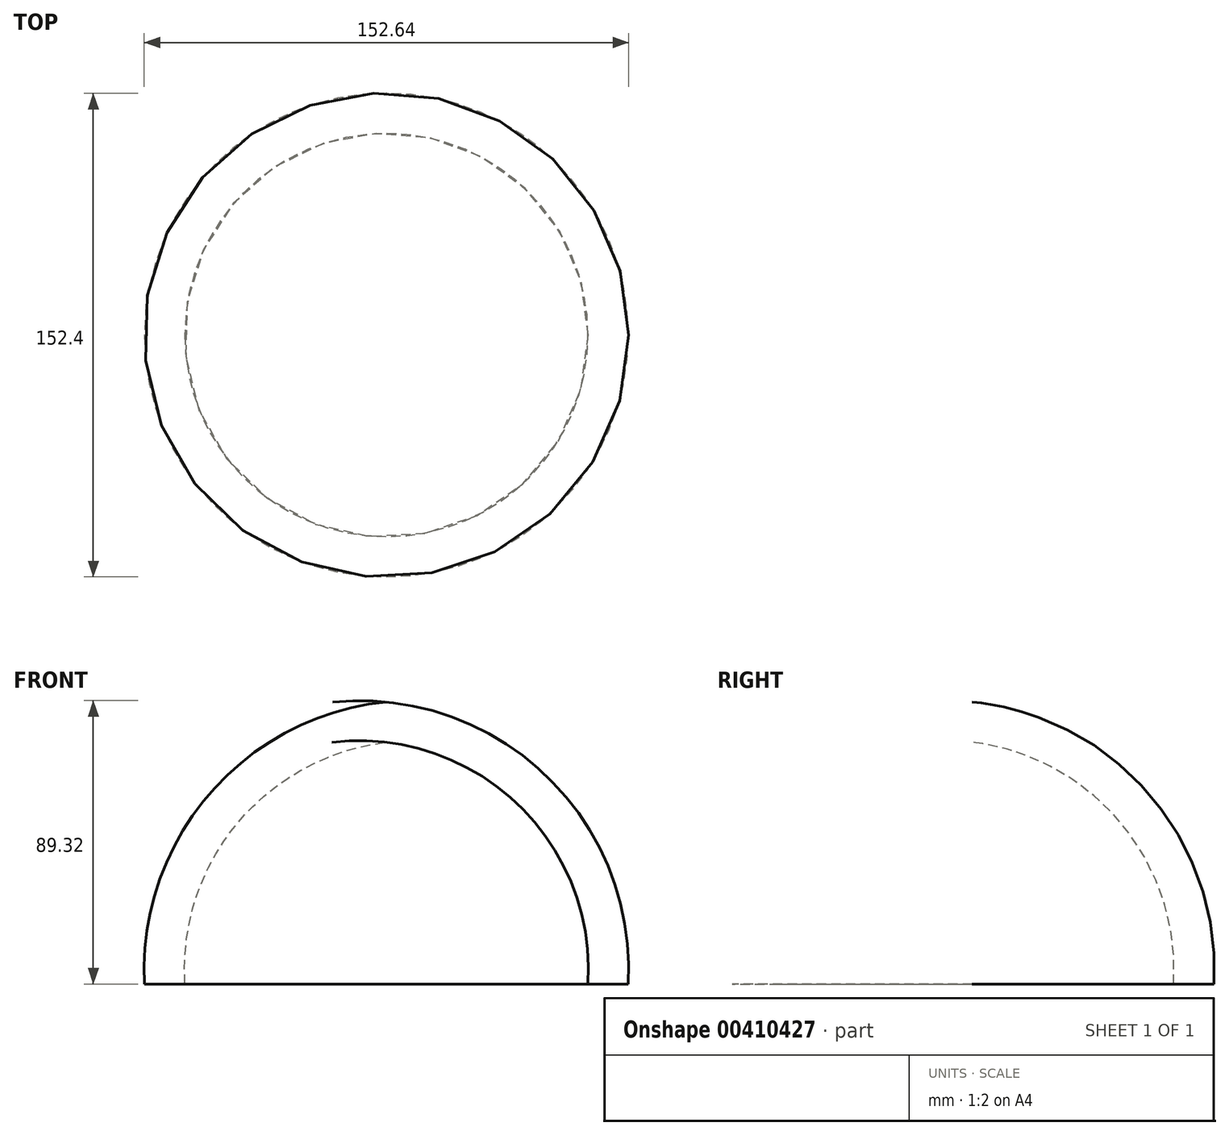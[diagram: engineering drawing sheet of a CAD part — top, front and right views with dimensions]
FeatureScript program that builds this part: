
annotation { "Feature Type Name" : "Feature", "Feature Type Description" : "" }
export const myFeature = defineFeature(function(context is Context, id is Id, definition is map)
    precondition{}
    {
        {
            var Q0;
            Q0=qCreatedBy(makeId("Front.planeOp"),FACE);
            var sketch = newSketch(context, id + "F0", { "sketchPlane" : qUnion([Q0])});
            skLineSegment(sketch, "E0", {"start": v(0, 76.2) * mm, "end": v(0, 88.9) * mm});
            skLineSegment(sketch, "E1", {"start": v(63.5, 0) * mm, "end": v(76.2, 0) * mm});
            skArc(sketch, "E2", {"start": v(76.2, 0) * mm, "mid": v(55.92, 59.72) * mm, "end": v(0, 88.9) * mm});
            skArc(sketch, "E3", {"start": v(63.5, 0) * mm, "mid": v(46.9, 50.72) * mm, "end": v(0, 76.2) * mm});
            skSolve(sketch);
        }
        {
            var Q0;
            Q0=makeQuery(id+"F0.imprint","IMPRINT",FACE,{"disambiguationData":[TD([[makeQuery(id+"F0.imprint","IMPRINT",EDGE,{"derivedFrom":sQuery(id+"F0.wireOp",EDGE,"E0")}),-1.0]])]});
            var Q1;
            Q1=sQuery(id+"F0.wireOp",EDGE,"E0");
            revolve(context, id + "F1", {"entities" : qUnion([Q0]), "axis" : qUnion([Q1]), "revolveType" : RevolveType.FULL});
        }
    });
